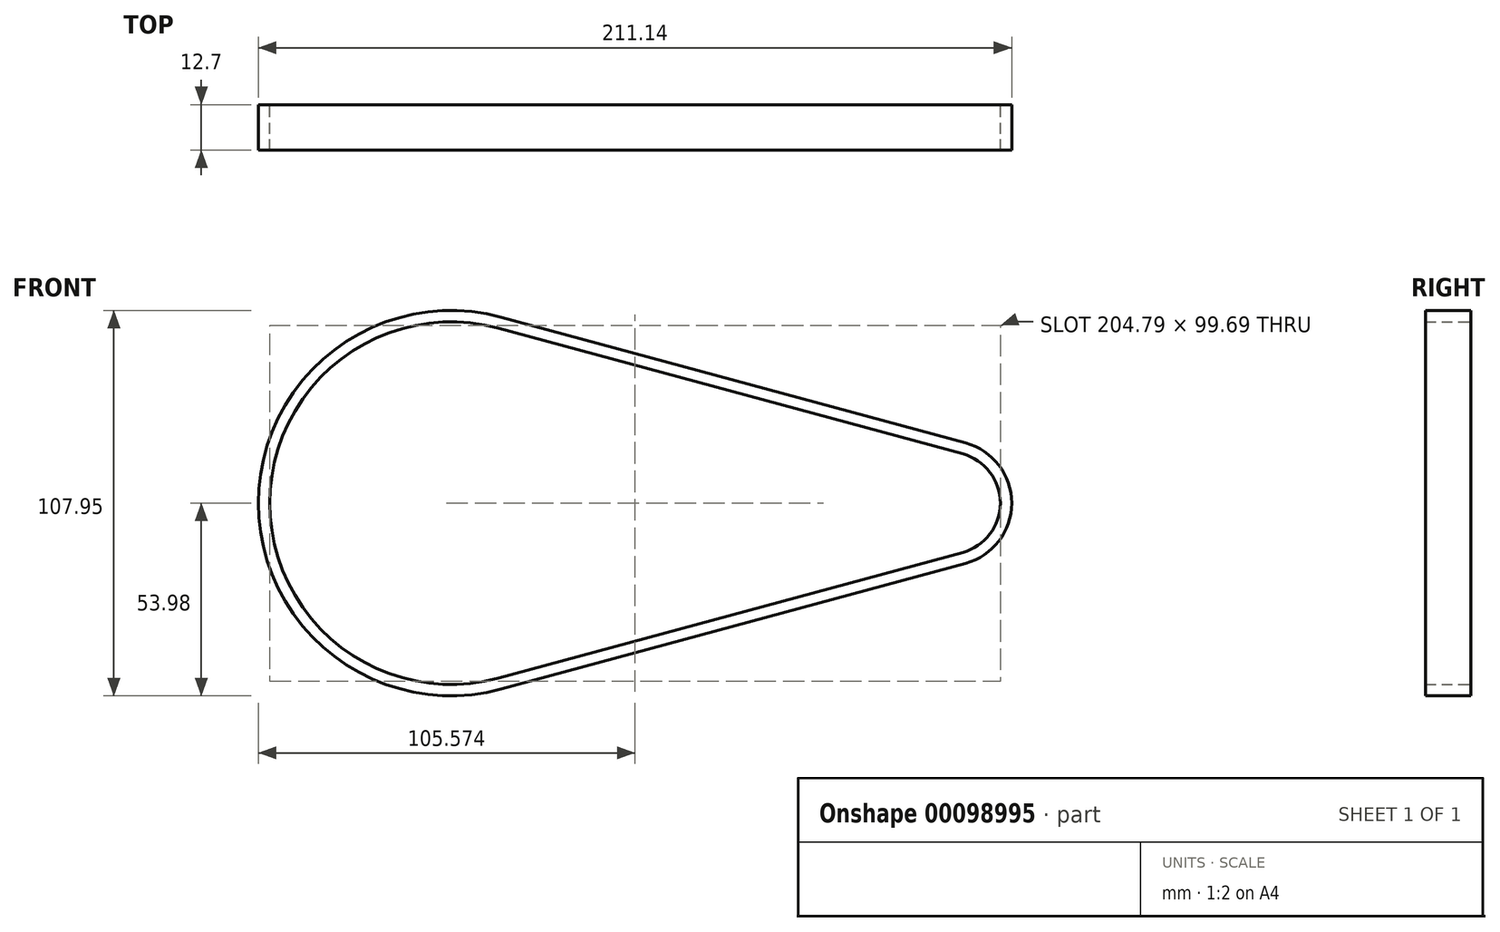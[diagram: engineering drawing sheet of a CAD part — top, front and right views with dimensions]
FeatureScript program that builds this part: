
annotation { "Feature Type Name" : "Feature", "Feature Type Description" : "" }
export const myFeature = defineFeature(function(context is Context, id is Id, definition is map)
    precondition{}
    {
        {
            var Q0;
            Q0=qCreatedBy(makeId("Front.planeOp"),FACE);
            var sketch = newSketch(context, id + "F0", { "sketchPlane" : qUnion([Q0])});
            skArc(sketch, "E0", {"start": v(13.28, 49.03) * mm, "mid": v(-50.8, 0) * mm, "end": v(13.28, -49.03) * mm});
            skArc(sketch, "E1", {"start": v(143.43, -13.8) * mm, "mid": v(153.99, 0) * mm, "end": v(143.43, 13.8) * mm});
            skLineSegment(sketch, "E2", {"start": v(13.28, 49.03) * mm, "end": v(143.43, 13.8) * mm});
            skLineSegment(sketch, "E3", {"start": v(13.28, -49.03) * mm, "end": v(143.43, -13.8) * mm});
            skArc(sketch, "E4.0", {"start": v(14.1, 52.1) * mm, "mid": v(-53.98, 0) * mm, "end": v(14.1, -52.1) * mm});
            skLineSegment(sketch, "E4.1", {"start": v(14.1, 52.1) * mm, "end": v(144.26, 16.86) * mm});
            skArc(sketch, "E4.2", {"start": v(144.26, -16.86) * mm, "mid": v(157.16, 0) * mm, "end": v(144.26, 16.86) * mm});
            skLineSegment(sketch, "E4.3", {"start": v(14.1, -52.1) * mm, "end": v(144.26, -16.86) * mm});
            skSolve(sketch);
        }
        {
            var Q0;
            Q0 = qSketchRegion(id + "F0", true);
            extrude(context, id + "F1", {"entities" : qUnion([Q0]), "depth" : 12.7 * mm});
        }
    });
